# Revit family: Sanitary_Basins_Cosentino_Exclusive 2
name_source: partatom
category: Plumbing Fixtures
units: mm (PartAtom-declared; Revit-internal decimal feet)

## family parameters
Always vertical = Yes
Cut with Voids When Loaded = No
Host = Wall
Part Type = Normal
Room Calculation Point = No
Round Connector Dimension = Use Diameter
Shared = No

## types (1)
- Exclusive One
    Assembly Code = D2010400
    CW Connection = No
    Default Elevation = 0 mm  [stored 0 ft]
    Description = The basin is one of the stars of your bathroom. Cosentino offers unique designs which fit smoothly into your room, your style, and the needs of your family.

Whether it’s for a master bathroom or a downstairs WC, we have the perfect product to transform your bathroom into a warm, welcoming space.
    Edition number = 1
    HW Connection = No
    Keynote = 10800
    Manufacturer = Cosentino
    Model = Exclusive One
    Product Guid = c8b579fd-9a26-4690-aca1-022a91911e97
    Product Material = Natural Stone - Cosentino - Silestone - Pietra - Suede
    Product data url = https://www.bimobject.com
    URL = www.cosentino.com
    Vent Connection = No
    Ι_Dstnc = 255 mm  [stored 0.836614 ft]
    Ι_Dstnc_1 = 220 mm
    Ι_Gnrc Mdl Optn 01 = Sinks_Cosentino_Integrity-One : Integrity ONE
    Ι_Typ Ntgr = 1

note: [stored X ft] marks values corroborated as IEEE doubles in the binary element streams (Revit-internal decimal feet)

## geometry (parser evidence)
native form markers: Sweep x9
no freeform markers — native parametric forms only
